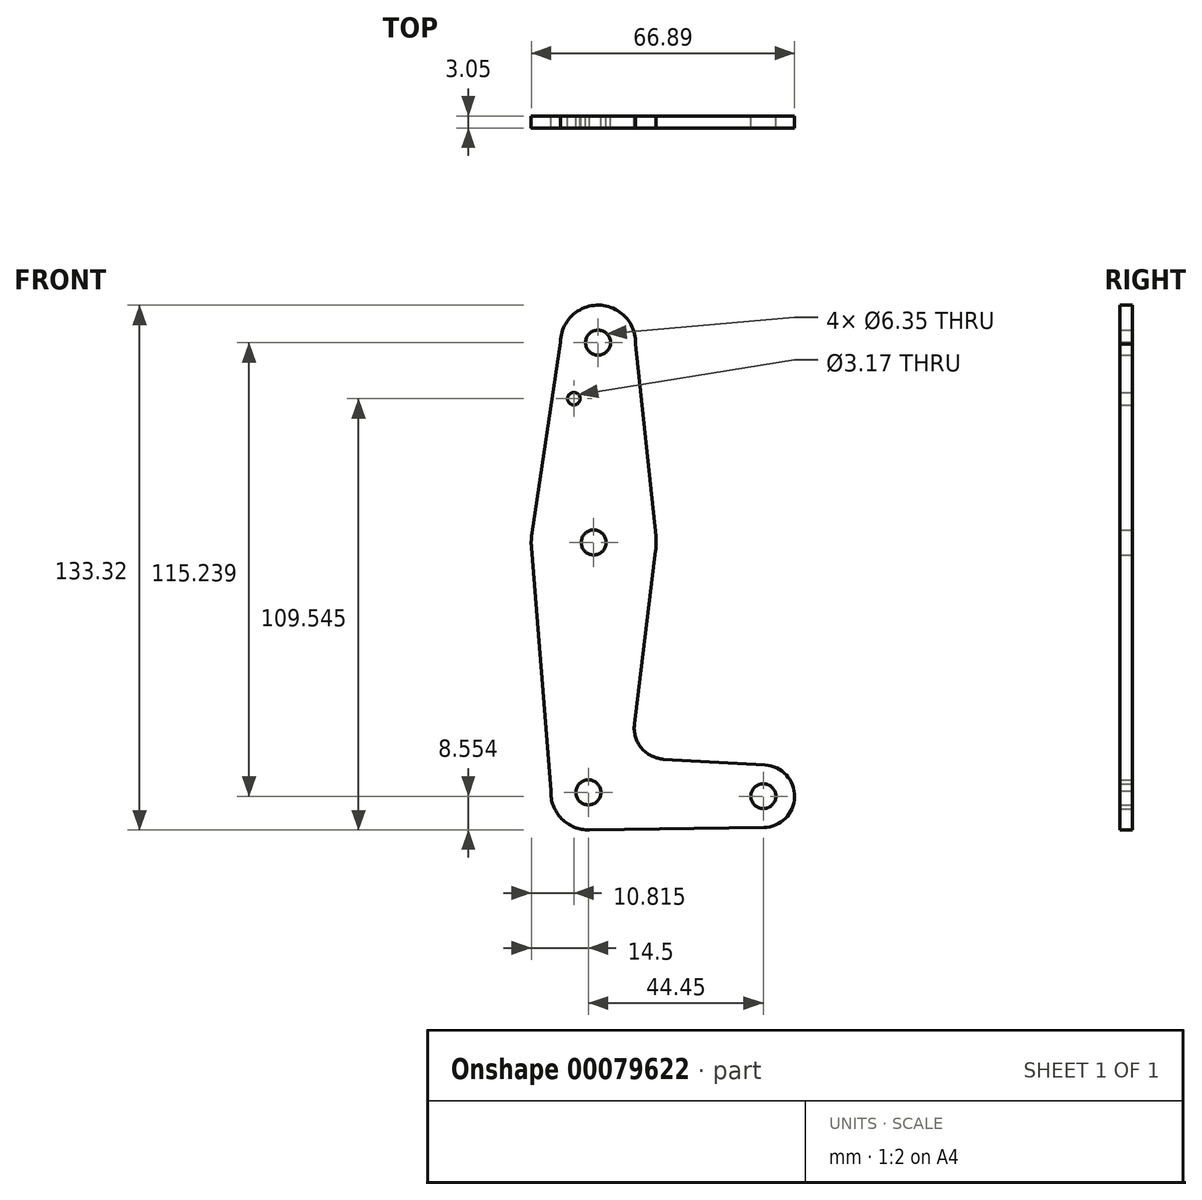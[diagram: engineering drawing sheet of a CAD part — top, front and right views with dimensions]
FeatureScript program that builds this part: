
annotation { "Feature Type Name" : "Feature", "Feature Type Description" : "" }
export const myFeature = defineFeature(function(context is Context, id is Id, definition is map)
    precondition{}
    {
        {
            var Q0;
            Q0=qCreatedBy(makeId("Front.planeOp"),FACE);
            var sketch = newSketch(context, id + "F0", { "sketchPlane" : qUnion([Q0])});
            skLineSegment(sketch, "E0", {"start": v(0, -40.66) * mm, "end": v(44.45, -41.63) * mm});
            skCircle(sketch, "E1", {"center": v(1.37, 22.84) * mm, "radius": 15.88 * mm});
            skCircle(sketch, "E2", {"center": v(0, -40.66) * mm, "radius": 9.53 * mm});
            skCircle(sketch, "E3", {"center": v(44.45, -41.63) * mm, "radius": 7.94 * mm});
            skLineSegment(sketch, "E4", {"start": v(2.47, 73.61) * mm, "end": v(0, -40.66) * mm});
            skLineSegment(sketch, "E5", {"start": v(-7.06, 73.72) * mm, "end": v(-14.33, 25.2) * mm});
            skLineSegment(sketch, "E6", {"start": v(11.99, 73.31) * mm, "end": v(17.16, 24.51) * mm});
            skLineSegment(sketch, "E7", {"start": v(17.12, 20.8) * mm, "end": v(11.72, -23.32) * mm});
            skLineSegment(sketch, "E8", {"start": v(-9.52, -40.26) * mm, "end": v(-14.45, 21.58) * mm});
            skLineSegment(sketch, "E9", {"start": v(19.15, -32.22) * mm, "end": v(44.9, -33.7) * mm});
            skLineSegment(sketch, "E10", {"start": v(0, -50.18) * mm, "end": v(44.56, -49.56) * mm});
            skCircle(sketch, "E11", {"center": v(1.37, 22.84) * mm, "radius": 3.18 * mm});
            skCircle(sketch, "E12", {"center": v(0, -40.66) * mm, "radius": 3.18 * mm});
            skCircle(sketch, "E13", {"center": v(44.45, -41.63) * mm, "radius": 3.18 * mm});
            skCircle(sketch, "E14", {"center": v(2.47, 73.61) * mm, "radius": 3.18 * mm});
            skCircle(sketch, "E15", {"center": v(2.47, 73.61) * mm, "radius": 9.53 * mm});
            skCircle(sketch, "E16", {"center": v(-3.69, 59.37) * mm, "radius": 1.59 * mm});
            skArc(sketch, "E17.filletArc", {"start": v(11.72, -23.32) * mm, "mid": v(13.5, -29.38) * mm, "end": v(19.15, -32.22) * mm});
            skSolve(sketch);
        }
        {
            var Q0;
            Q0 = qSketchRegion(id + "F0", true);
            var Q1;
            {var subQ0=sQuery(id+"F0.wireOp",EDGE,"E12");var subQ1=sQuery(id+"F0.wireOp",EDGE,"E0");var subQ2=makeQuery(id+"F0.imprint","INTERSECT",VERTEX,{"derivedFrom":[subQ1,subQ0]});Q1=makeQuery(id+"F0.imprint","IMPRINT",FACE,{"disambiguationData":[TD([[makeQuery(id+"F0.imprint","IMPRINT",EDGE,{"disambiguationData":[TD([[subQ2,-1.0]])],"derivedFrom":subQ1}),1.0]])]});}
            extrude(context, id + "F1", {"entities" : qUnion([Q0, Q1]), "depth" : 3.05 * mm});
        }
    });
